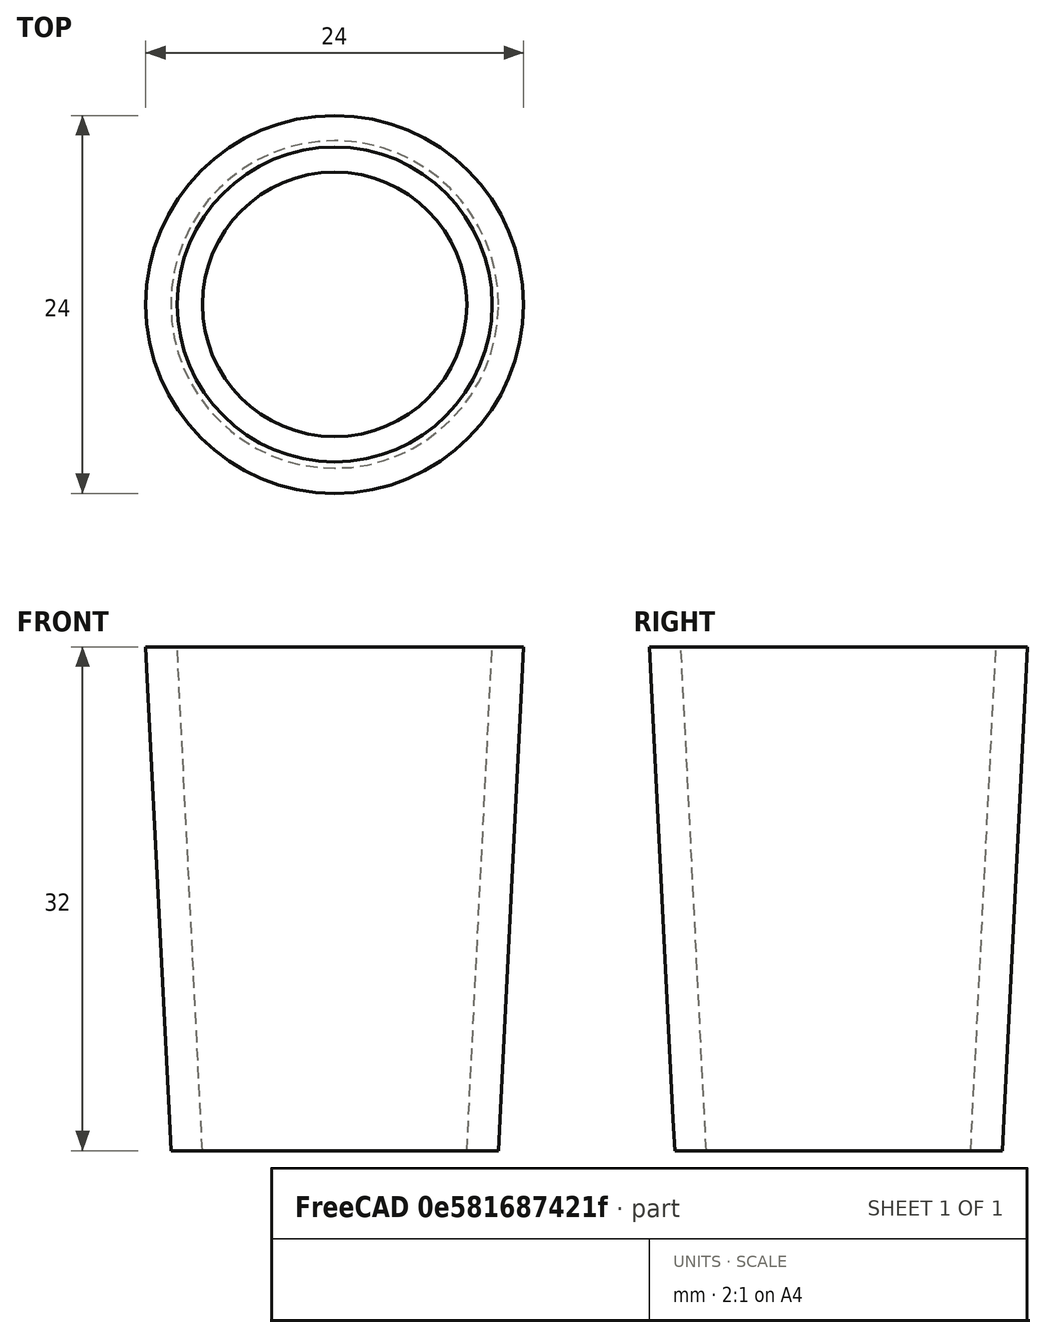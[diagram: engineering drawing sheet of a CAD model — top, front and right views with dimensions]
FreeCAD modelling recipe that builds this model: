
FCSTD DOCUMENT  (FreeCAD 1.0R1.0.2)
Label: ISO383_Joints
License: All rights reserved
LicenseURL: http://en.wikipedia.org/wiki/All_rights_reserved
objects: Part::Cone×3, Spreadsheet::Sheet×1, Part::MultiFuse×1, Part::Cut×1
note: 5 computed .brp shape members not serialized (recipe doc carries the construction recipe); baked Part::Feature solids carry a one-line shape summary decoded from their .brp

FEATURE [Spreadsheet::Sheet] Spreadsheet  label="ISO383"
  Flange = 24
  cells = A1='Nominal joint diameter; B1='l; C1='h1; D1='h2; E1='Major diameter; G1='Nonstandard properties for the model(s); A2==hiddenref(.Flange.String); B2(joint_l)==.B27; C2(joint_h1)==.C27; D2(joint_h2)==.D27; E2(joint_d1)==.E27; G2='Wall thickness (Glass); H2(thickness)=2; A3='18.8 (k2 18.8/8); B3=8; C3=2.5; D3=2; E3=18.8; G3='Minor diameter; H3(joint_d2)==joint_d1 - (joint_l + joint_h1 + joint_h2) / 10; A4='24 (k2 24/9); B4=9; C4=2.5; D4=2; E4=24; G4='Diameter ground zone 1; H4(diameter_gz1)==joint_d1 - joint_h1 / 10; A5='29.5 (k2 29.5/10); B5=10; C5=2.5; D5=2; E5=29.5; G5='Diameter ground zone 2; H5(diameter_gz2)==joint_d1 - (joint_l + joint_h1) / 10; A6='34.5 (k2 34.5/11); B6=11; C6=2.5; D6=2; E6=34.5; A7='40 (k2 40/11); B7=11; C7=2.5; D7=2.5; E7=40; A8='45 (k2 45/11); B8=11; C8=2.5; D8=2.5; E8=45; A9='50 (k2 50/12); B9=12; C9=2.5; D9=2.5; E9=50; A10='5 (k4 5/8); B10=8; C10=2; D10=2; E10=5; A11='7.5 (k4 7.5/10); B11=10; C11=2; D11=2; E11=7.5; A12='10 (k4 10/12); B12=12; C12=2; D12=2; E12=10; A13='12.5 (k4 12.5/13); B13=13; C13=2; D13=2; E13=12.5; A14='14.5 (k4 14.5/14); B14=14; C14=2; D14=2; E14=14.5; A15='18.8 (k4 18.8/16); B15=16; C15=2; D15=2; E15=18.8; A16='21.5 (k4 21.5/18); B16=18; C16=2; D16=2; E16=21.5; A17='24 (k4 24/19); B17=19; C17=2; D17=2; E17=24; A18='29.5 (k4 19.5/21); B18=21; C18=2; D18=2; E18=29.5; A19='34.5 (k4 34.5/22); B19=22; C19=2; D19=2; E19=34.5; A20='5 (k6 5/12); B20=12; C20=2; D20=2; E20=5; A21='7.5 (k6 7.5/15); B21=15; C21=2; D21=2; E21=7.5; A22='10 (k6 10/18); B22=18; C22=2; D22=2; E22=10; A23='12.5 (k6 12.5/20); B23=20; C23=2; D23=2; E23=12.5; A24='14.5 (k6 14.5/22); B24=22; C24=2; D24=2; E24=14.5; A25='18.8 (k6 18.8/25); B25=25; C25=2; D25=2; E25=18.8; A26='21.5 (k6 21.5/27); B26=27; C26=2; D26=2; E26=21.5; A27='24 (k6 24/28); B27=28; C27=2; D27=2; E27=24; A28='29.5 (k6 29.5/31); B28=31; C28=2; D28=2; E28=29.5; A29='34.5 (k6 34.5/34); B29=34; C29=2; D29=2; E29=34.5; A30='40 (k6 40/37); B30=37; C30=2; D30=2; E30=40; A31='45 (k6 45/39); B31=39; C31=2; D31=2; E31=45; A32='50 (k6 50/41); B32=41; C32=2; D32=3; E32=50; A33='60 (k6 60/45); B33=45; C33=2; D33=3; E33=60; A34='71 (k6 71/50); B34=50; C34=2; D34=3; E34=71; A35='85 (k6 85/54); B35=54; C35=2; D35=3; E35=85; A36='100 (k6 100/59); B36=59; C36=2; D36=3; E36=100; A37='5 (k8 5/17); B37=17; C37=2.5; D37=2; E37=5; A38='7.5 (k8 7.5/21); B38=21; C38=2.5; D38=2; E38=7.5; A39='10 (k8 10/24); +39 more cells
  expr: .Flange.Enum = cells[<<A3:|>>]
  expr: .cells.Bind.B2.E2 = tuple(.cells; <<B>> + str(hiddenref(Flange) + 3); <<E>> + str(hiddenref(Flange) + 3))
FEATURE [Part::Cone] Cone
  Angle = 360
  AttacherType = Attacher::AttachEngine3D
  Height = 32
  Radius1 = 10.4
  Radius2 = 12
  expr: Height = <<ISO383>>.joint_h1 + <<ISO383>>.joint_h2 + <<ISO383>>.joint_l
  expr: Radius1 = <<ISO383>>.joint_d2 / 2
  expr: Radius2 = <<ISO383>>.joint_d1 / 2
FEATURE [Part::Cone] Cone001
  Angle = 360
  AttacherType = Attacher::AttachEngine3D
  Height = 32
  Radius1 = 8.4
  Radius2 = 10
  expr: Height = <<ISO383>>.joint_h1 + <<ISO383>>.joint_h2 + <<ISO383>>.joint_l
  expr: Radius1 = <<ISO383>>.joint_d2 / 2 - <<ISO383>>.thickness
  expr: Radius2 = <<ISO383>>.joint_d1 / 2 - <<ISO383>>.thickness
FEATURE [Part::Cone] Cone002  label="GroundZone"
  Angle = 360
  AttacherType = Attacher::AttachEngine3D
  Height = 28
  Placement = pos=(0,0,2) rot=(0,0,1;0rad)
  Radius1 = 10.5
  Radius2 = 11.9
  expr: .Placement.Base.z = <<ISO383>>.joint_h2
  expr: Height = <<ISO383>>.joint_l
  expr: Radius1 = <<ISO383>>.diameter_gz2 / 2
  expr: Radius2 = <<ISO383>>.diameter_gz1 / 2
FEATURE [Part::MultiFuse] Fusion
  Shapes = -> [Cone,Cone002]
FEATURE [Part::Cut] Cut  label="IS383_Joint"
  Base = -> Fusion
  Tool = -> Cone001
